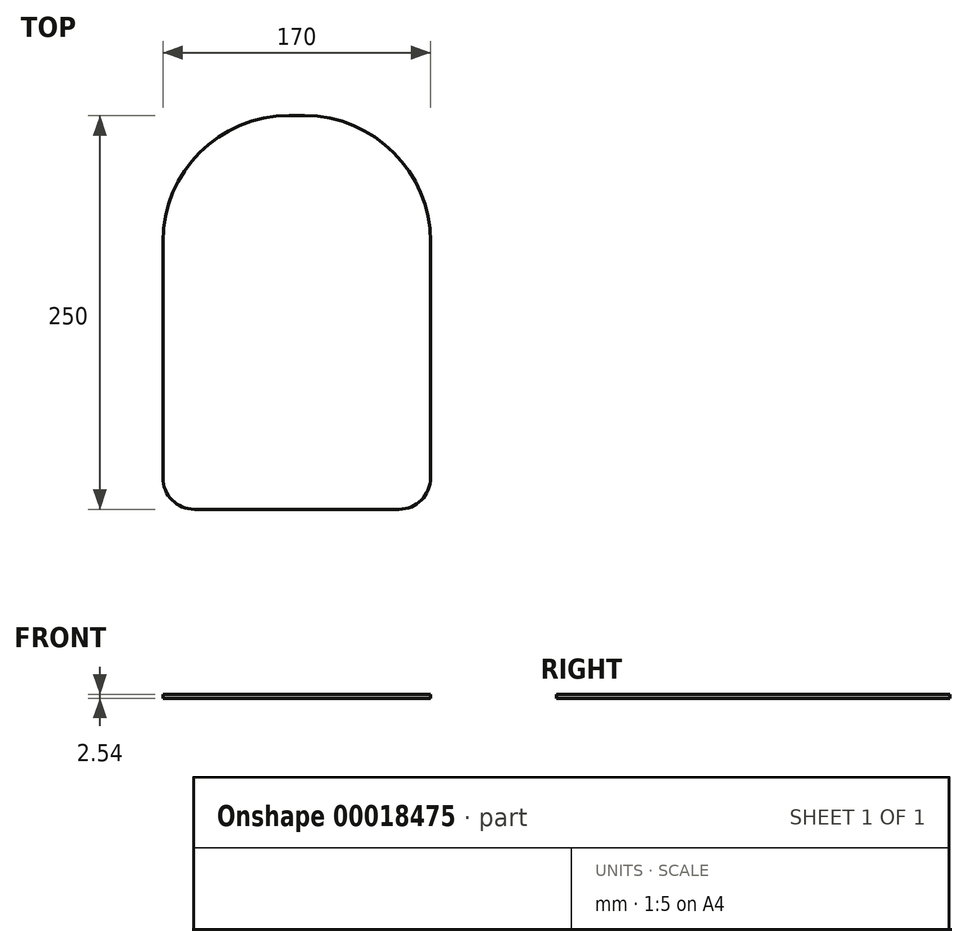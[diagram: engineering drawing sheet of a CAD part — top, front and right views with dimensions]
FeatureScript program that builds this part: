
annotation { "Feature Type Name" : "Feature", "Feature Type Description" : "" }
export const myFeature = defineFeature(function(context is Context, id is Id, definition is map)
    precondition{}
    {
        {
            var Q0;
            Q0=qCreatedBy(makeId("Top.planeOp"),FACE);
            var sketch = newSketch(context, id + "F0", { "sketchPlane" : qUnion([Q0])});
            skLineSegment(sketch, "E0.rect.bottom", {"start": v(65, -125) * mm, "end": v(-65, -125) * mm});
            skLineSegment(sketch, "E0.rect.top", {"start": v(5, 125) * mm, "end": v(-5, 125) * mm});
            skLineSegment(sketch, "E0.rect.left", {"start": v(85, -105) * mm, "end": v(85, 45) * mm});
            skLineSegment(sketch, "E0.rect.right", {"start": v(-85, -105) * mm, "end": v(-85, 45) * mm});
            skPoint(sketch, "E0.rect.middle", {"position": v(0, 0) * mm});
            skPoint(sketch, "E1.visualSharp", {"position": v(85, -125) * mm});
            skArc(sketch, "E1.filletArc", {"start": v(65, -125) * mm, "mid": v(79.14, -119.14) * mm, "end": v(85, -105) * mm});
            skPoint(sketch, "E2.visualSharp", {"position": v(-85, -125) * mm});
            skArc(sketch, "E2.filletArc", {"start": v(-85, -105) * mm, "mid": v(-79.14, -119.14) * mm, "end": v(-65, -125) * mm});
            skPoint(sketch, "E3.visualSharp", {"position": v(-85, 125) * mm});
            skArc(sketch, "E3.filletArc", {"start": v(-5, 125) * mm, "mid": v(-61.57, 101.57) * mm, "end": v(-85, 45) * mm});
            skPoint(sketch, "E4.visualSharp", {"position": v(85, 125) * mm});
            skArc(sketch, "E4.filletArc", {"start": v(85, 45) * mm, "mid": v(61.57, 101.57) * mm, "end": v(5, 125) * mm});
            skSolve(sketch);
        }
        {
            var Q0;
            Q0=qSketchRegion(id+"F0",true);
            extrude(context, id + "F1", {"entities" : qUnion([Q0]), "depth" : 2.54 * mm});
        }
    });
